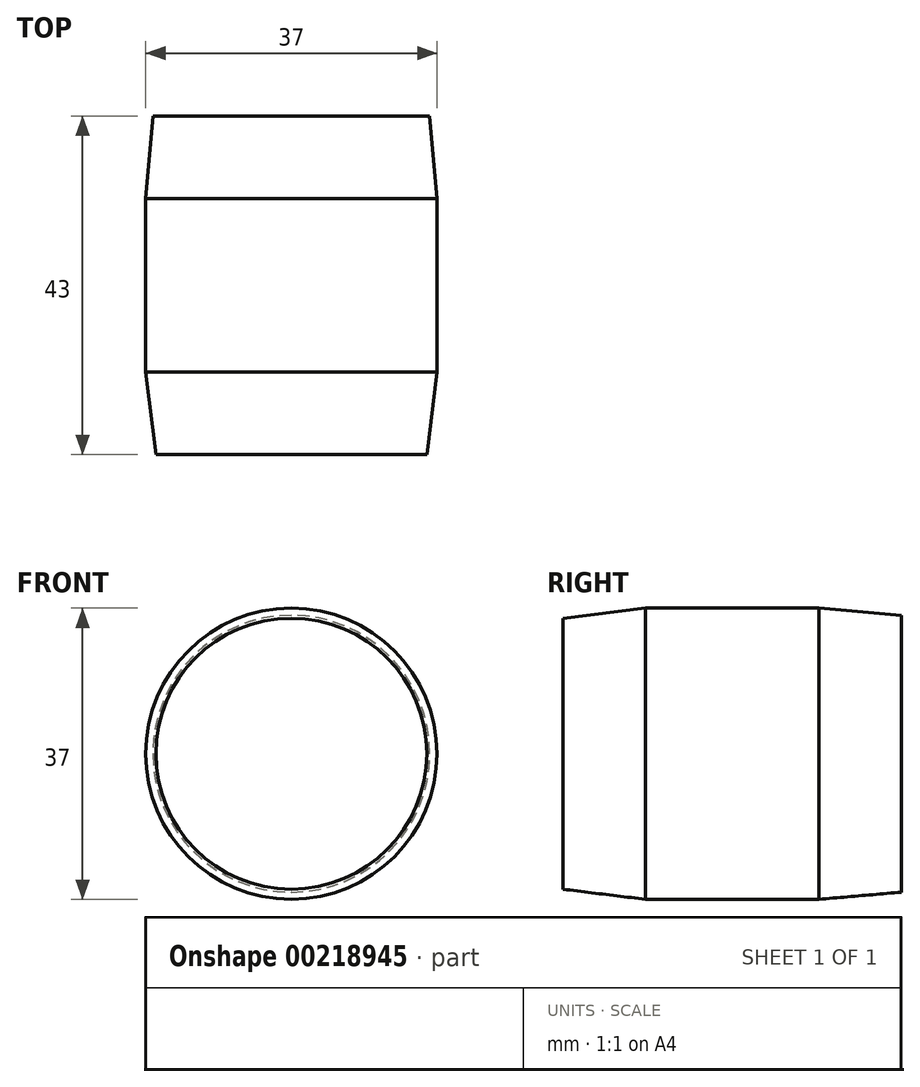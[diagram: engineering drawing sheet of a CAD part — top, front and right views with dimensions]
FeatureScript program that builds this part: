
annotation { "Feature Type Name" : "Feature", "Feature Type Description" : "" }
export const myFeature = defineFeature(function(context is Context, id is Id, definition is map)
    precondition{}
    {
        {
            var Q0;
            Q0=qCreatedBy(makeId("Front.planeOp"),FACE);
            var sketch = newSketch(context, id + "F0", { "sketchPlane" : qUnion([Q0])});
            skCircle(sketch, "E0", {"center": v(0, 0) * mm, "radius": 18.5 * mm});
            skSolve(sketch);
        }
        {
            var Q0;
            Q0 = qSketchRegion(id + "F0", true);
            extrude(context, id + "F1", {"entities" : qUnion([Q0]), "oppositeDirection" : true, "depth" : 22 * mm});
        }
        {
            assignVariable(context, id + "F2", {"name" : "cap", "anyValue" : (43 - 22) / 2});
        }
        {
            var Q0;
            Q0=makeQuery(id+"F1.opExtrude","CAP_FACE",FACE,{"disambiguationData":[OSD([sQuery(id+"F0.wireOp",EDGE,"E0")])],"isStart":true});
            var sketch = newSketch(context, id + "F3", { "sketchPlane" : qUnion([Q0])});
            skCircle(sketch, "E1", {"center": v(0, 0) * mm, "radius": 15 * mm});
            skSolve(sketch);
        }
        {
            var Q0;
            Q0=makeQuery(id+"F3.imprint","IMPRINT",FACE,{"disambiguationData":[TD([[makeQuery(id+"F3.imprint","IMPRINT",EDGE,{"derivedFrom":sQuery(id+"F3.wireOp",EDGE,"E1")}),-1.0]])]});
            var Q1;
            Q1=makeQuery(id+"F3.imprint","IMPRINT",FACE,{"disambiguationData":[TD([[makeQuery(id+"F3.imprint","IMPRINT",EDGE,{"derivedFrom":sQuery(id+"F3.wireOp",EDGE,"E1")}),1.0]])]});
            extrude(context, id + "F4", {"entities" : qUnion([Q0, Q1]), "operationType" : NewBodyOperationType.ADD, "depth" : (getVariable(context, 'cap')) * mm, "hasDraft" : true, "draftAngle" : 7 * degree, "draftPullDirection" : true});
        }
        {
            var Q0;
            Q0=makeQuery(id+"F1.opExtrude","CAP_FACE",FACE,{"disambiguationData":[OSD([sQuery(id+"F0.wireOp",EDGE,"E0")])],"isStart":false});
            extrude(context, id + "F5", {"entities" : qUnion([Q0]), "operationType" : NewBodyOperationType.ADD, "depth" : (getVariable(context, 'cap')) * mm, "hasDraft" : true, "draftAngle" : 5 * degree, "draftPullDirection" : true});
        }
    });
